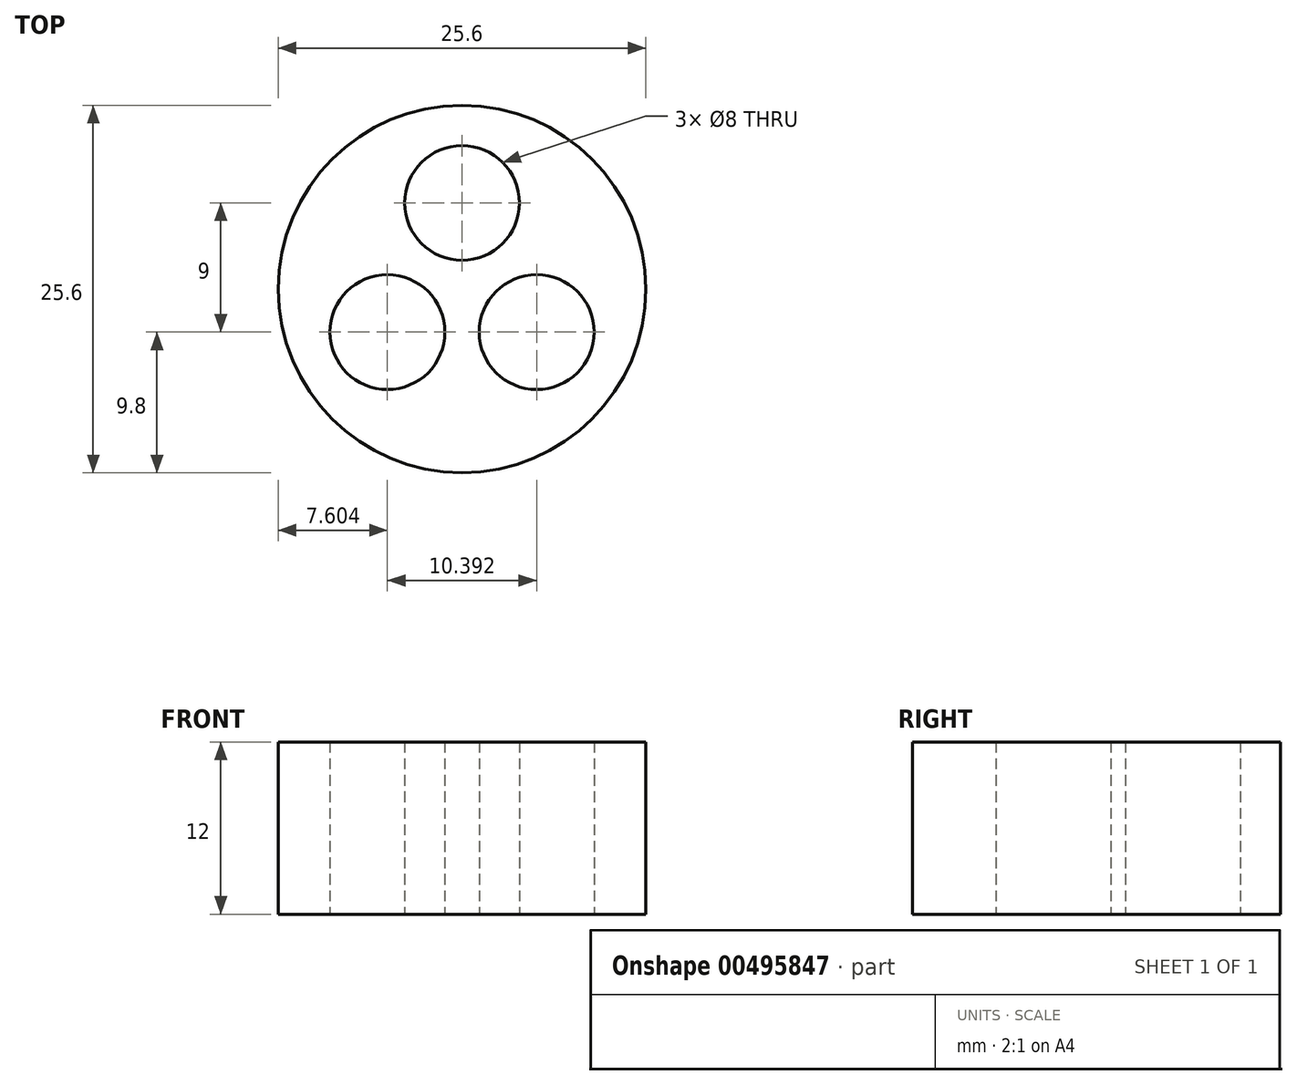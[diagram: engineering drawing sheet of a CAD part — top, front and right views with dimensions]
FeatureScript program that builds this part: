
annotation { "Feature Type Name" : "Feature", "Feature Type Description" : "" }
export const myFeature = defineFeature(function(context is Context, id is Id, definition is map)
    precondition{}
    {
        {
            var Q0;
            Q0=qCreatedBy(makeId("Top.planeOp"),FACE);
            var sketch = newSketch(context, id + "F0", { "sketchPlane" : qUnion([Q0])});
            skCircle(sketch, "E0", {"center": v(0, 0) * mm, "radius": 12.8 * mm});
            skCircle(sketch, "E1", {"center": v(0, 6) * mm, "radius": 4 * mm});
            skCircle(sketch, "E2.1.0", {"center": v(-5.2, -3) * mm, "radius": 4 * mm});
            skCircle(sketch, "E2.2.0", {"center": v(5.2, -3) * mm, "radius": 4 * mm});
            skSolve(sketch);
        }
        {
            var Q0;
            Q0=qSketchRegion(id+"F0",true);
            extrude(context, id + "F1", {"entities" : qUnion([Q0]), "depth" : 12 * mm});
        }
    });
